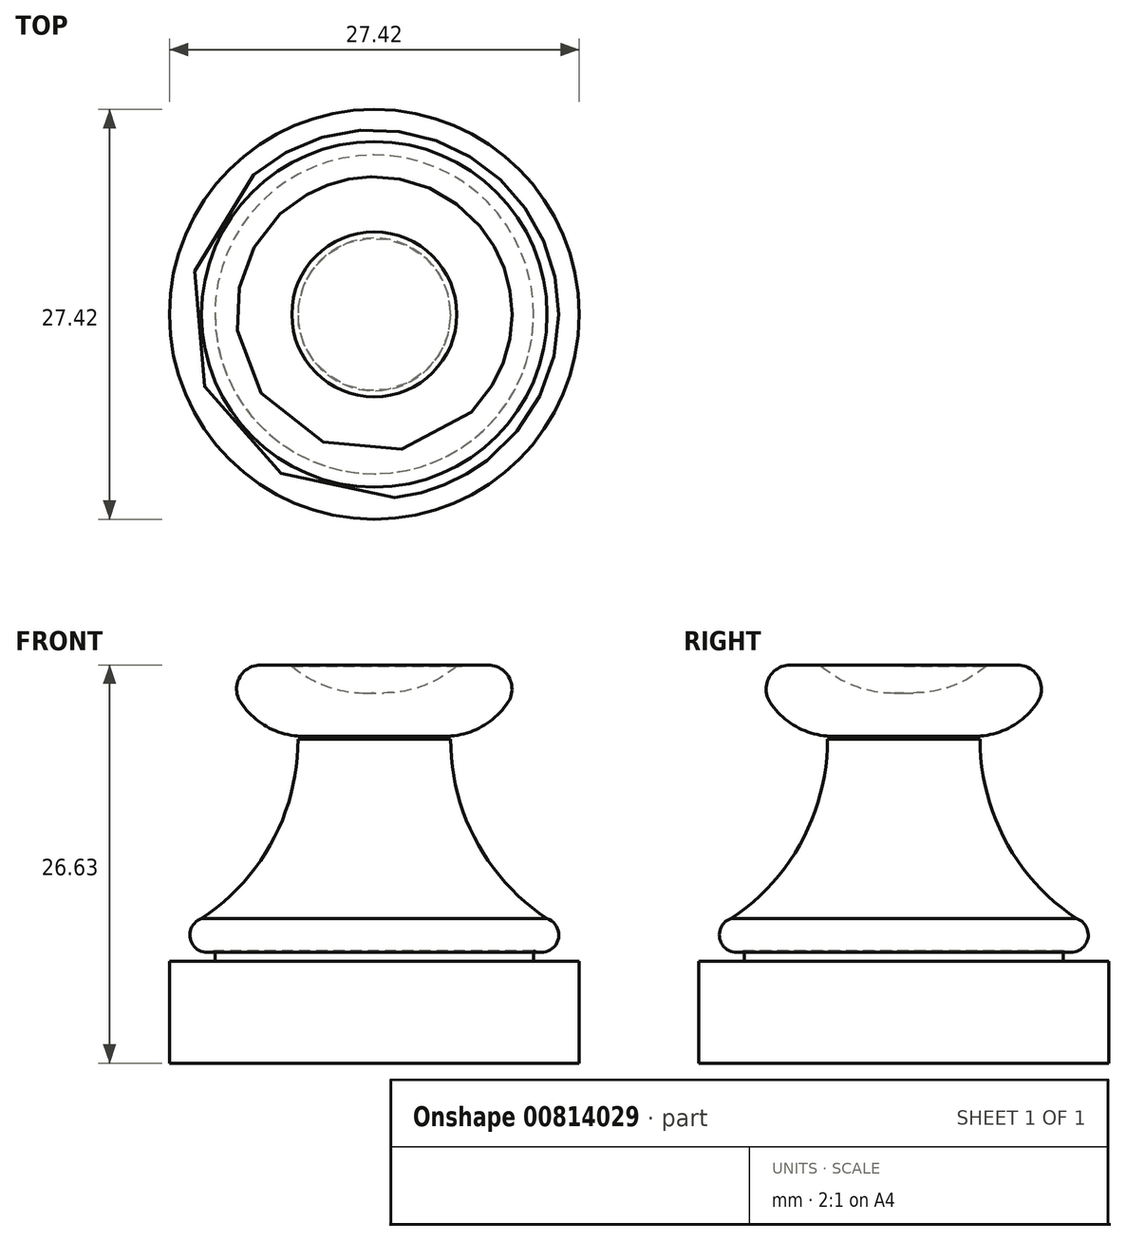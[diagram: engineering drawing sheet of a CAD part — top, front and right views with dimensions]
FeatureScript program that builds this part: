
annotation { "Feature Type Name" : "Feature", "Feature Type Description" : "" }
export const myFeature = defineFeature(function(context is Context, id is Id, definition is map)
    precondition{}
    {
        {
            var Q0;
            Q0=qCreatedBy(makeId("Front.planeOp"),FACE);
            var sketch = newSketch(context, id + "F0", { "sketchPlane" : qUnion([Q0])});
            skLineSegment(sketch, "E0", {"start": v(0, 0) * mm, "end": v(-13.7, 0) * mm});
            skLineSegment(sketch, "E1", {"start": v(-13.7, 0) * mm, "end": v(-13.7, 6.8) * mm});
            skLineSegment(sketch, "E2", {"start": v(-13.7, 6.8) * mm, "end": v(0, 6.8) * mm});
            skLineSegment(sketch, "E3", {"start": v(0, 6.8) * mm, "end": v(0, 0) * mm});
            skSolve(sketch);
        }
        {
            var Q0;
            Q0 = qSketchRegion(id + "F0", true);
            var Q1;
            Q1=sQuery(id+"F0.wireOp",EDGE,"E3");
            revolve(context, id + "F1", {"surfaceOperationType" : NewSurfaceOperationType.NEW, "entities" : qUnion([Q0]), "axis" : qUnion([Q1]), "revolveType" : RevolveType.FULL});
        }
        {
            var Q0;
            Q0=qCreatedBy(makeId("Front.planeOp"),FACE);
            var sketch = newSketch(context, id + "F2", { "sketchPlane" : qUnion([Q0])});
            skArc(sketch, "E4", {"start": v(-11.56, 9.68) * mm, "mid": v(-12.25, 8.13) * mm, "end": v(-10.66, 7.53) * mm});
            skArc(sketch, "E5", {"start": v(-11.56, 9.68) * mm, "mid": v(-6.81, 14.86) * mm, "end": v(-5.1, 21.68) * mm});
            skLineSegment(sketch, "E6", {"start": v(-5.1, 21.68) * mm, "end": v(0, 21.68) * mm});
            skLineSegment(sketch, "E7", {"start": v(0, 21.68) * mm, "end": v(0, 6.63) * mm});
            skLineSegment(sketch, "E8", {"start": v(0, 6.63) * mm, "end": v(-10.66, 6.63) * mm});
            skLineSegment(sketch, "E9", {"start": v(-10.66, 7.53) * mm, "end": v(-10.66, 6.63) * mm});
            skSolve(sketch);
        }
        {
            var Q0;
            Q0 = qSketchRegion(id + "F2", true);
            var Q1;
            Q1=sQuery(id+"F2.wireOp",EDGE,"E7");
            revolve(context, id + "F3", {"operationType" : NewBodyOperationType.ADD, "surfaceOperationType" : NewSurfaceOperationType.NEW, "entities" : qUnion([Q0]), "axis" : qUnion([Q1]), "revolveType" : RevolveType.FULL});
        }
        {
            var Q0;
            Q0=qCreatedBy(makeId("Front.planeOp"),FACE);
            var sketch = newSketch(context, id + "F4", { "sketchPlane" : qUnion([Q0])});
            skLineSegment(sketch, "E10", {"start": v(-4.75, 21.86) * mm, "end": v(-9.78, 21.86) * mm});
            skLineSegment(sketch, "E11", {"start": v(-9.78, 21.86) * mm, "end": v(-9.78, 26.7) * mm});
            skLineSegment(sketch, "E12", {"start": v(-9.78, 26.7) * mm, "end": v(-4.21, 26.52) * mm});
            skLineSegment(sketch, "E13", {"start": v(-4.21, 26.52) * mm, "end": v(0, 26.52) * mm});
            skLineSegment(sketch, "E14", {"start": v(0, 26.52) * mm, "end": v(0, 21.86) * mm});
            skLineSegment(sketch, "E15", {"start": v(0, 21.86) * mm, "end": v(-4.75, 21.86) * mm});
            skSolve(sketch);
        }
        {
            var Q0;
            Q0 = qSketchRegion(id + "F4", true);
            var Q1;
            Q1=sQuery(id+"F4.wireOp",EDGE,"E14");
            revolve(context, id + "F5", {"surfaceOperationType" : NewSurfaceOperationType.NEW, "entities" : qUnion([Q0]), "axis" : qUnion([Q1]), "revolveType" : RevolveType.FULL});
        }
        {
            var Q0;
            Q0=qCreatedBy(makeId("Front.planeOp"),FACE);
            var sketch = newSketch(context, id + "F6", { "sketchPlane" : qUnion([Q0])});
            skArc(sketch, "E16", {"start": v(0, 39.8) * mm, "mid": v(-7.68, 34.95) * mm, "end": v(-5.11, 26.24) * mm});
            skLineSegment(sketch, "E17", {"start": v(-5.11, 26.24) * mm, "end": v(0, 26.24) * mm});
            skLineSegment(sketch, "E18", {"start": v(0, 26.24) * mm, "end": v(0, 39.8) * mm});
            skSolve(sketch);
        }
        {
            var Q0;
            Q0 = qSketchRegion(id + "F6", true);
            var Q1;
            Q1=sQuery(id+"F6.wireOp",EDGE,"E18");
            revolve(context, id + "F7", {"operationType" : NewBodyOperationType.ADD, "surfaceOperationType" : NewSurfaceOperationType.NEW, "entities" : qUnion([Q0]), "axis" : qUnion([Q1]), "revolveType" : RevolveType.FULL});
        }
        {
            var Q0;
            Q0=makeQuery(id+"F5.opRevolve","SWEPT_EDGE",EDGE,{"disambiguationData":[OSD([sQuery(id+"F4.wireOp",EDGE,"E10"),sQuery(id+"F4.wireOp",EDGE,"E11")])]});
            fillet(context, id + "F8", {"entities" : qUnion([Q0]), "radius" : 5.08 * mm, "tangentPropagation" : true, "allowEdgeOverflow" : false});
        }
        {
            var Q0;
            Q0=makeQuery(id+"F8.opFillet","BLEND_EDGE",EDGE,{"blendedFrom":[makeQuery(id+"F5.opRevolve","SWEPT_EDGE",EDGE,{"disambiguationData":[OSD([sQuery(id+"F4.wireOp",EDGE,"E10"),sQuery(id+"F4.wireOp",EDGE,"E11")])]}),makeQuery(id+"F5.opRevolve","SWEPT_FACE",FACE,{"disambiguationData":[OSD([sQuery(id+"F4.wireOp",EDGE,"E12")])]})],"blendedInto":[makeQuery(id+"F5.opRevolve","SWEPT_FACE",FACE,{"disambiguationData":[OSD([sQuery(id+"F4.wireOp",EDGE,"E12")])]})]});
            fillet(context, id + "F9", {"entities" : qUnion([Q0]), "radius" : 1.6 * mm, "tangentPropagation" : true, "allowEdgeOverflow" : false});
        }
    });
